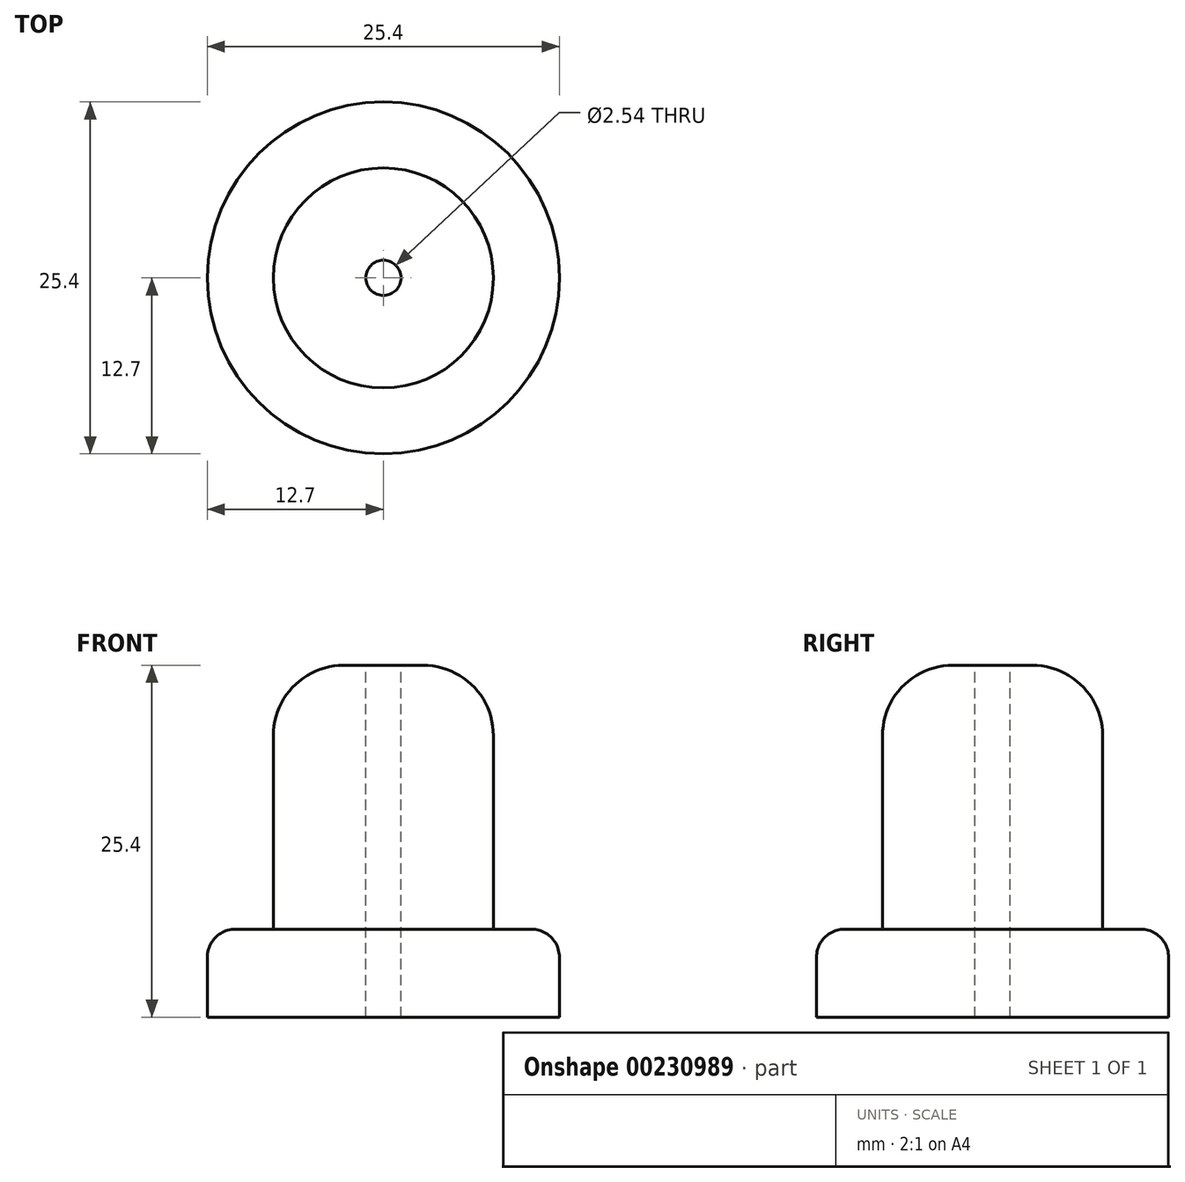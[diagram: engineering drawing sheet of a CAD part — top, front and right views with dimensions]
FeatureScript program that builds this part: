
annotation { "Feature Type Name" : "Feature", "Feature Type Description" : "" }
export const myFeature = defineFeature(function(context is Context, id is Id, definition is map)
    precondition{}
    {
        {
            var Q0;
            Q0=qCreatedBy(makeId("Top.planeOp"),FACE);
            var sketch = newSketch(context, id + "F0", { "sketchPlane" : qUnion([Q0])});
            skCircle(sketch, "E0", {"center": v(0, 0) * mm, "radius": 7.94 * mm});
            skSolve(sketch);
        }
        {
            var Q0;
            Q0=qCreatedBy(makeId("Top.planeOp"),FACE);
            var sketch = newSketch(context, id + "F1", { "sketchPlane" : qUnion([Q0])});
            skCircle(sketch, "E1", {"center": v(0, 0) * mm, "radius": 12.7 * mm});
            skSolve(sketch);
        }
        {
            var Q0;
            Q0=makeQuery(id+"F0.imprint","IMPRINT",FACE,{"disambiguationData":[TD([[makeQuery(id+"F0.imprint","IMPRINT",EDGE,{"derivedFrom":sQuery(id+"F0.wireOp",EDGE,"E0")}),1.0]])]});
            extrude(context, id + "F2", {"entities" : qUnion([Q0]), "depth" : 25.4 * mm});
        }
        {
            var Q0;
            Q0=makeQuery(id+"F1.imprint","IMPRINT",FACE,{"disambiguationData":[TD([[makeQuery(id+"F1.imprint","IMPRINT",EDGE,{"derivedFrom":sQuery(id+"F1.wireOp",EDGE,"E1")}),1.0]])]});
            extrude(context, id + "F3", {"entities" : qUnion([Q0]), "operationType" : NewBodyOperationType.ADD, "depth" : 6.35 * mm});
        }
        {
            var Q0;
            Q0=makeQuery(id+"F2.opExtrude","CAP_EDGE",EDGE,{"disambiguationData":[OSD([sQuery(id+"F0.wireOp",EDGE,"E0")])],"isStart":false});
            fillet(context, id + "F4", {"entities" : qUnion([Q0]), "radius" : 5.08 * mm, "tangentPropagation" : true, "allowEdgeOverflow" : false});
        }
        {
            var Q0;
            Q0=makeQuery(id+"F3.opExtrude","CAP_EDGE",EDGE,{"disambiguationData":[OSD([sQuery(id+"F1.wireOp",EDGE,"E1")])],"isStart":false});
            fillet(context, id + "F5", {"entities" : qUnion([Q0]), "radius" : 2.03 * mm, "tangentPropagation" : true, "allowEdgeOverflow" : false});
        }
        {
            var Q0;
            Q0=makeQuery(id+"F2.opExtrude","CAP_FACE",FACE,{"disambiguationData":[OSD([sQuery(id+"F0.wireOp",EDGE,"E0")])],"isStart":false});
            var sketch = newSketch(context, id + "F6", { "sketchPlane" : qUnion([Q0])});
            skCircle(sketch, "E2", {"center": v(0, 0) * mm, "radius": 1.27 * mm});
            skSolve(sketch);
        }
        {
            var Q0;
            Q0=makeQuery(id+"F6.imprint","IMPRINT",FACE,{"disambiguationData":[TD([[makeQuery(id+"F6.imprint","IMPRINT",EDGE,{"derivedFrom":sQuery(id+"F6.wireOp",EDGE,"E2")}),1.0]])]});
            extrude(context, id + "F7", {"entities" : qUnion([Q0]), "operationType" : NewBodyOperationType.REMOVE, "oppositeDirection" : true, "depth" : 38.1 * mm});
        }
    });
